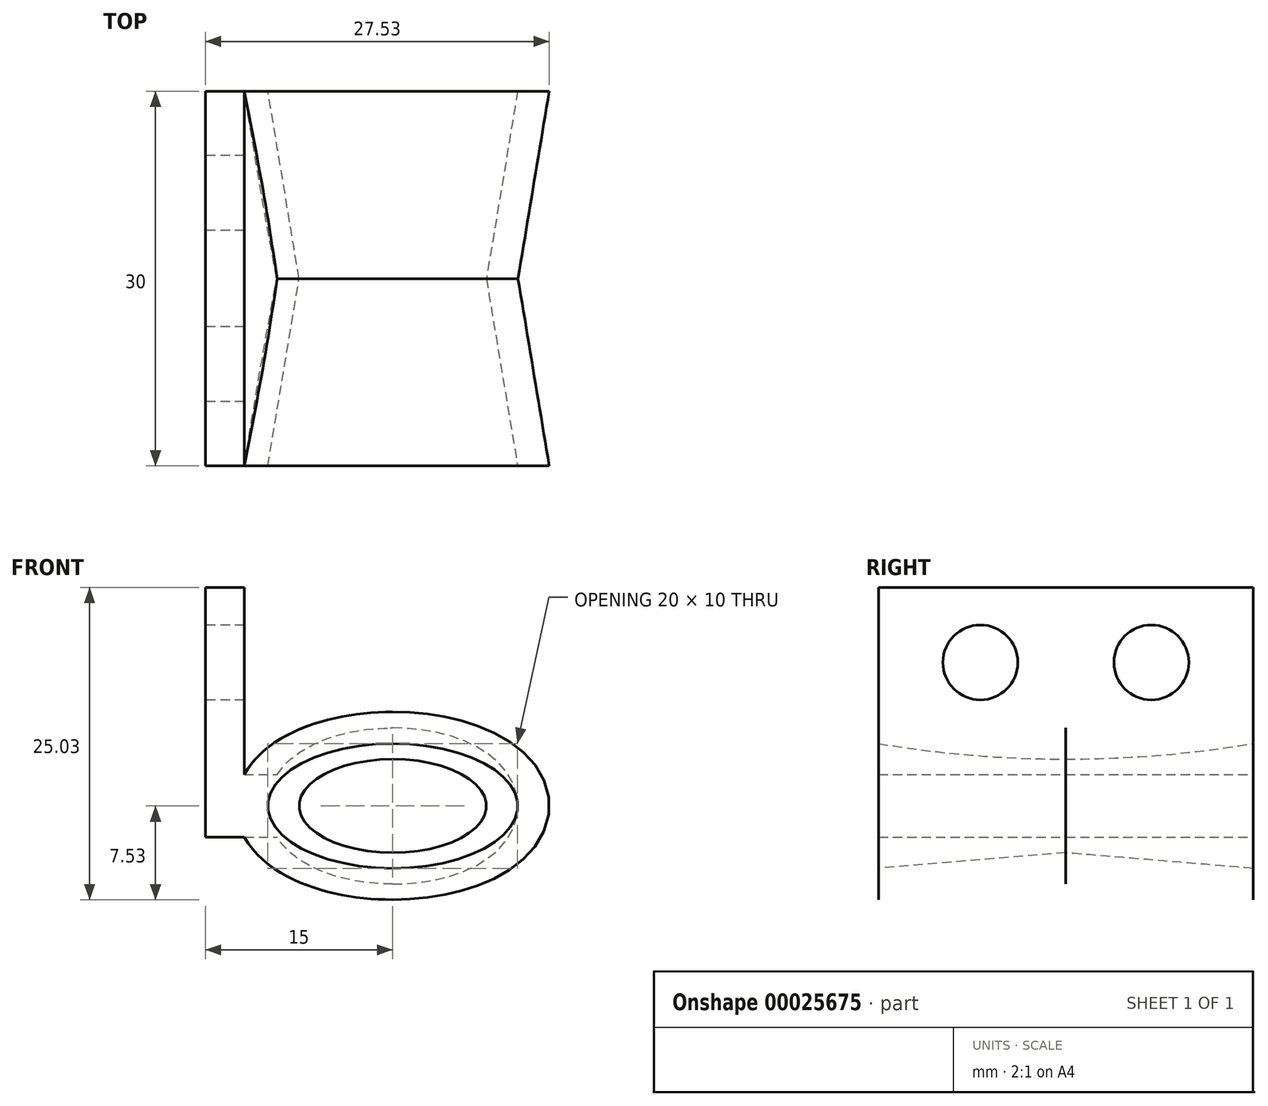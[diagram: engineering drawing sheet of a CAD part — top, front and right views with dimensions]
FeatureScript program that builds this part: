
annotation { "Feature Type Name" : "Feature", "Feature Type Description" : "" }
export const myFeature = defineFeature(function(context is Context, id is Id, definition is map)
    precondition{}
    {
        {
            var Q0;
            Q0=qCreatedBy(makeId("Front.planeOp"),FACE);
            var sketch = newSketch(context, id + "F0", { "sketchPlane" : qUnion([Q0])});
            skEllipticalArc(sketch, "E0", {});
            skLineSegment(sketch, "E1", {"start": v(0, -3.75) * mm, "end": v(0, 3.75) * mm});
            const initialGuessF0  = {"E0": [0, 0, 1, 0, 0.0075, 0.00375, 4.71238898038469, 1.5707963267948966]};
            skSetInitialGuess(sketch, initialGuessF0);
            skSolve(sketch);
        }
        {
            var Q0;
            Q0=qCreatedBy(makeId("Front.planeOp"),FACE);
            cPlane(context, id + "F1", {"entities" : qUnion([Q0]), "cplaneType" : CPlaneType.OFFSET, "offset" : 15 * mm, "width" : 150 * mm, "height" : 150 * mm});
        }
        {
            var Q0;
            Q0=qCreatedBy(id+"F1.planeOp",FACE);
            var sketch = newSketch(context, id + "F2", { "sketchPlane" : qUnion([Q0])});
            skEllipticalArc(sketch, "E2", {});
            skLineSegment(sketch, "E3", {"start": v(0, -5) * mm, "end": v(0, 5) * mm});
            const initialGuessF2  = {"E2": [0, 0, 1, 0, 0.01, 0.005, 4.71238898038469, 1.5707963267948966]};
            skSetInitialGuess(sketch, initialGuessF2);
            skSolve(sketch);
        }
        {
            var Q0;
            Q0=qCreatedBy(makeId("Right.planeOp"),FACE);
            var sketch = newSketch(context, id + "F3", { "sketchPlane" : qUnion([Q0])});
            skArc(sketch, "E4", {"start": v(-15, 5) * mm, "mid": v(-7.53, 4.06) * mm, "end": v(0, 3.75) * mm});
            skSolve(sketch);
        }
        {
            var Q0;
            Q0=makeQuery(id+"F0.imprint","IMPRINT",FACE,{"disambiguationData":[TD([[makeQuery(id+"F0.imprint","IMPRINT",EDGE,{"derivedFrom":sQuery(id+"F0.wireOp",EDGE,"E0")}),1.0]])]});
            var Q1;
            Q1=makeQuery(id+"F2.imprint","IMPRINT",FACE,{"disambiguationData":[TD([[makeQuery(id+"F2.imprint","IMPRINT",EDGE,{"derivedFrom":sQuery(id+"F2.wireOp",EDGE,"E2")}),1.0]])]});
            var Q2;
            Q2=qBodyType(qCreatedBy(id+"F3",EDGE),BodyType.WIRE);
            loft(context, id + "F4", {"addGuides" : true, "sheetProfilesArray" : [{ "sheetProfileEntities" : qUnion([Q0]) }, { "sheetProfileEntities" : qUnion([Q1]) }], "guidesArray" : [{ "guideEntities" : qUnion([Q2]), "guideDerivativeType" : LoftGuideDerivativeType.DEFAULT, "guideDerivativeMagnitude" : 1 }]});
        }
        {
            var Q0;
            Q0=makeQuery(id+"F4.opLoft","SWEPT_BODY",BODY,{"disambiguationData":[OSD([makeQuery(id+"F0.imprint","IMPRINT",FACE,{"disambiguationData":[TD([[makeQuery(id+"F0.imprint","IMPRINT",EDGE,{"derivedFrom":sQuery(id+"F0.wireOp",EDGE,"E0")}),1.0]])]}),makeQuery(id+"F2.imprint","IMPRINT",FACE,{"disambiguationData":[TD([[makeQuery(id+"F2.imprint","IMPRINT",EDGE,{"derivedFrom":sQuery(id+"F2.wireOp",EDGE,"E2")}),1.0]])]}),sQuery(id+"F3.wireOp",EDGE,"E4")])]});
            var Q1;
            Q1=qCreatedBy(makeId("Right.planeOp"),FACE);
            mirror(context, id + "F5", {"operationType" : NewBodyOperationType.ADD, "entities" : qUnion([Q0]), "mirrorPlane" : qUnion([Q1])});
        }
        {
            var Q0;
            Q0=makeQuery(id+"F4.opLoft","SWEPT_BODY",BODY,{"disambiguationData":[OSD([makeQuery(id+"F0.imprint","IMPRINT",FACE,{"disambiguationData":[TD([[makeQuery(id+"F0.imprint","IMPRINT",EDGE,{"derivedFrom":sQuery(id+"F0.wireOp",EDGE,"E0")}),1.0]])]}),makeQuery(id+"F2.imprint","IMPRINT",FACE,{"disambiguationData":[TD([[makeQuery(id+"F2.imprint","IMPRINT",EDGE,{"derivedFrom":sQuery(id+"F2.wireOp",EDGE,"E2")}),1.0]])]}),sQuery(id+"F3.wireOp",EDGE,"E4")])]});
            var Q1;
            Q1=qCreatedBy(makeId("Front.planeOp"),FACE);
            mirror(context, id + "F6", {"operationType" : NewBodyOperationType.ADD, "entities" : qUnion([Q0]), "mirrorPlane" : qUnion([Q1])});
        }
        {
            var Q0;
            {var subQ0=makeQuery(id+"F4.opLoft","CAP_FACE",FACE,{"disambiguationData":[OSD([makeQuery(id+"F2.imprint","IMPRINT",FACE,{"disambiguationData":[TD([[makeQuery(id+"F2.imprint","IMPRINT",EDGE,{"derivedFrom":sQuery(id+"F2.wireOp",EDGE,"E2")}),1.0]])]})])],"isStart":true});Q0=makeQuery(id+"F5.boolean.opBoolean","MERGE",FACE,{"derivedFrom":[subQ0,makeQuery(id+"F5.opPattern","COPY",FACE,{"derivedFrom":subQ0,"instanceName":"1"})]});}
            var Q1;
            {var subQ0=makeQuery(id+"F4.opLoft","CAP_FACE",FACE,{"disambiguationData":[OSD([makeQuery(id+"F2.imprint","IMPRINT",FACE,{"disambiguationData":[TD([[makeQuery(id+"F2.imprint","IMPRINT",EDGE,{"derivedFrom":sQuery(id+"F2.wireOp",EDGE,"E2")}),1.0]])]})])],"isStart":true});Q1=makeQuery(id+"F6.opPattern","COPY",FACE,{"derivedFrom":makeQuery(id+"F5.boolean.opBoolean","MERGE",FACE,{"derivedFrom":[subQ0,makeQuery(id+"F5.opPattern","COPY",FACE,{"derivedFrom":subQ0,"instanceName":"1"})]}),"instanceName":"1"});}
            shell(context, id + "F7", {"entities" : qUnion([Q0, Q1]), "thickness" : 2.5 * mm, "oppositeDirection" : true});
        }
        {
            var Q0;
            Q0=qCreatedBy(makeId("Right.planeOp"),FACE);
            cPlane(context, id + "F8", {"entities" : qUnion([Q0]), "cplaneType" : CPlaneType.OFFSET, "offset" : 15 * mm, "oppositeDirection" : true, "width" : 150 * mm, "height" : 150 * mm});
        }
        {
            var Q0;
            Q0=qCreatedBy(id+"F8.planeOp",FACE);
            var sketch = newSketch(context, id + "F9", { "sketchPlane" : qUnion([Q0])});
            skLineSegment(sketch, "E5.bottom", {"start": v(15, -2.5) * mm, "end": v(-15, -2.5) * mm});
            skLineSegment(sketch, "E5.top", {"start": v(15, 2.5) * mm, "end": v(-15, 2.5) * mm});
            skLineSegment(sketch, "E5.left", {"start": v(15, -2.5) * mm, "end": v(15, 2.5) * mm});
            skLineSegment(sketch, "E5.right", {"start": v(-15, -2.5) * mm, "end": v(-15, 2.5) * mm});
            skSolve(sketch);
        }
        {
            var Q0;
            Q0=qSketchRegion(id+"F9",true);
            extrude(context, id + "F10", {"entities" : qUnion([Q0]), "operationType" : NewBodyOperationType.ADD, "endBound" : BoundingType.UP_TO_NEXT, "depth" : 25 * mm});
        }
        {
            var Q0;
            Q0=makeQuery(id+"F10.opExtrude","SWEPT_FACE",FACE,{"disambiguationData":[OSD([sQuery(id+"F9.wireOp",EDGE,"E5.top")])]});
            var sketch = newSketch(context, id + "F11", { "sketchPlane" : qUnion([Q0])});
            skLineSegment(sketch, "E6.bottom", {"start": v(-15, -15) * mm, "end": v(-11.9, -15) * mm});
            skLineSegment(sketch, "E6.top", {"start": v(-15, 15) * mm, "end": v(-11.9, 15) * mm});
            skLineSegment(sketch, "E6.left", {"start": v(-15, -15) * mm, "end": v(-15, 15) * mm});
            skLineSegment(sketch, "E6.right", {"start": v(-11.9, -15) * mm, "end": v(-11.9, 15) * mm});
            skSolve(sketch);
        }
        {
            var Q0;
            Q0=qSketchRegion(id+"F11",true);
            extrude(context, id + "F12", {"entities" : qUnion([Q0]), "operationType" : NewBodyOperationType.ADD, "depth" : 15 * mm});
        }
        {
            var Q0;
            Q0=makeQuery(id+"F12.boolean.opBoolean","MERGE",FACE,{"derivedFrom":[makeQuery(id+"F10.opExtrude","CAP_FACE",FACE,{"disambiguationData":[OSD([sQuery(id+"F9.wireOp",EDGE,"E5.bottom"),sQuery(id+"F9.wireOp",EDGE,"E5.top"),sQuery(id+"F9.wireOp",EDGE,"E5.left"),sQuery(id+"F9.wireOp",EDGE,"E5.right")])],"isStart":true}),makeQuery(id+"F12.opExtrude","SWEPT_FACE",FACE,{"disambiguationData":[OSD([sQuery(id+"F11.wireOp",EDGE,"E6.left")])]})]});
            var sketch = newSketch(context, id + "F13", { "sketchPlane" : qUnion([Q0])});
            skPoint(sketch, "E7", {"position": v(6.85, 11.5) * mm});
            skLineSegment(sketch, "E8", {"start": v(0, 0) * mm, "end": v(0, 17.5) * mm, "construction": true});
            skPoint(sketch, "E9.MirrorP", {"position": v(-6.85, 11.5) * mm});
            skSolve(sketch);
        }
        {
            var Q0;
            Q0=sQuery(id+"F13.wireOp",VERTEX,"E7");
            var Q1;
            Q1=sQuery(id+"F13.wireOp",VERTEX,"E9.MirrorP");
            var Q2;
            Q2=makeQuery(id+"F4.opLoft","SWEPT_BODY",BODY,{"disambiguationData":[OSD([makeQuery(id+"F0.imprint","IMPRINT",FACE,{"disambiguationData":[TD([[makeQuery(id+"F0.imprint","IMPRINT",EDGE,{"derivedFrom":sQuery(id+"F0.wireOp",EDGE,"E0")}),1.0]])]}),makeQuery(id+"F2.imprint","IMPRINT",FACE,{"disambiguationData":[TD([[makeQuery(id+"F2.imprint","IMPRINT",EDGE,{"derivedFrom":sQuery(id+"F2.wireOp",EDGE,"E2")}),1.0]])]}),sQuery(id+"F3.wireOp",EDGE,"E4")])]});
            hole(context, id + "F14", {"style" : HoleStyle.SIMPLE, "holeDiameter" : 6 * mm, "endStyle" : HoleEndStyle.THROUGH, "locations" : qUnion([Q0, Q1]), "scope" : qUnion([Q2])});
        }
    });
